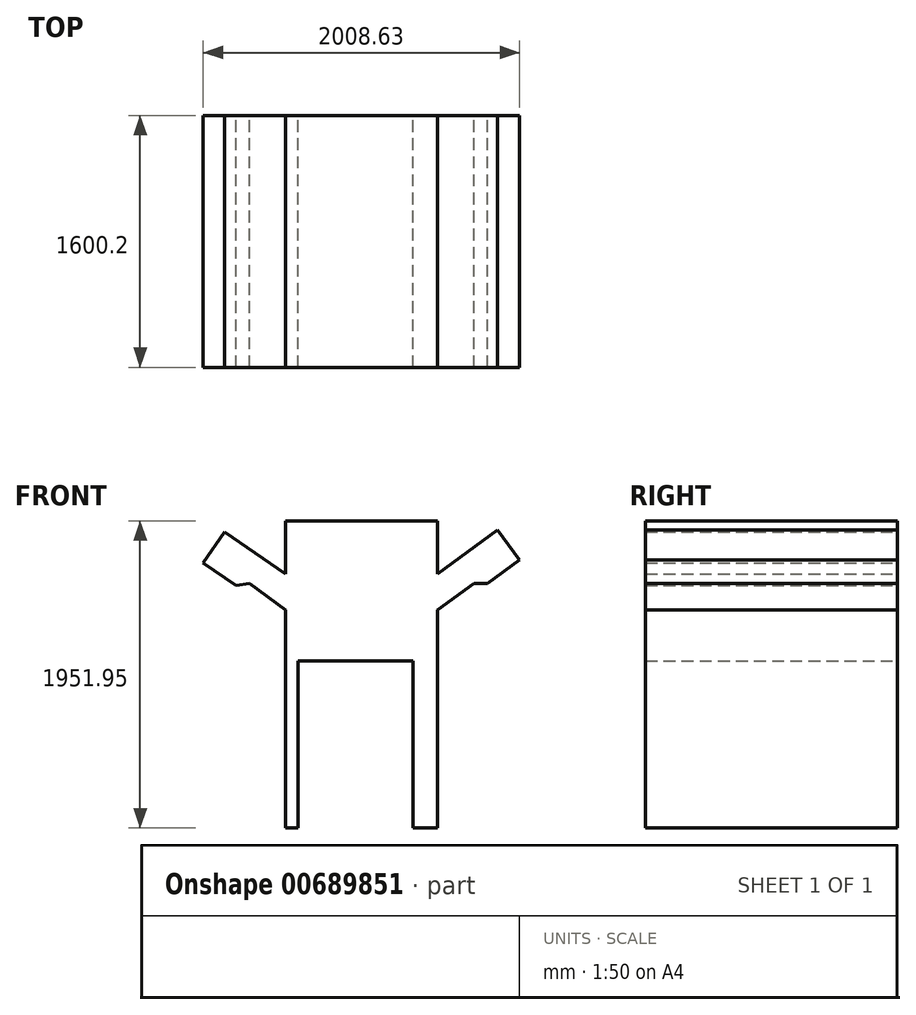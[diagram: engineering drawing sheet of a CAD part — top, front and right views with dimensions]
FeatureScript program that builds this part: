
annotation { "Feature Type Name" : "Feature", "Feature Type Description" : "" }
export const myFeature = defineFeature(function(context is Context, id is Id, definition is map)
    precondition{}
    {
        {
            var Q0;
            Q0=qCreatedBy(makeId("Front.planeOp"),FACE);
            var sketch = newSketch(context, id + "F0", { "sketchPlane" : qUnion([Q0])});
            skLineSegment(sketch, "E0", {"start": v(0, 0) * mm, "end": v(0, 1500) * mm, "construction": true});
            skLineSegment(sketch, "E1.bottom", {"start": v(-1147.27, 0) * mm, "end": v(-1302.33, 0) * mm});
            skLineSegment(sketch, "E1.top", {"start": v(-1147.27, 1951.95) * mm, "end": v(-2112.47, 1951.95) * mm});
            skLineSegment(sketch, "E1.left", {"start": v(-1147.27, 0) * mm, "end": v(-1147.27, 1384.3) * mm});
            skLineSegment(sketch, "E1.right", {"start": v(-2112.47, 0) * mm, "end": v(-2112.47, 1384.3) * mm});
            skLineSegment(sketch, "E2", {"start": v(-1147.27, 1384.3) * mm, "end": v(-917.57, 1554.27) * mm});
            skLineSegment(sketch, "E3", {"start": v(-917.57, 1554.27) * mm, "end": v(-831.16, 1552.95) * mm});
            skLineSegment(sketch, "E4", {"start": v(-831.16, 1552.95) * mm, "end": v(-626.98, 1704.03) * mm});
            skLineSegment(sketch, "E5", {"start": v(-626.98, 1704.03) * mm, "end": v(-767.5, 1893.92) * mm});
            skLineSegment(sketch, "E6", {"start": v(-767.5, 1893.92) * mm, "end": v(-1147.27, 1612.9) * mm});
            skLineSegment(sketch, "E7", {"start": v(-2112.47, 1612.9) * mm, "end": v(-2501.82, 1880.5) * mm});
            skLineSegment(sketch, "E8", {"start": v(-2501.82, 1880.5) * mm, "end": v(-2635.61, 1685.82) * mm});
            skLineSegment(sketch, "E9", {"start": v(-2635.61, 1685.82) * mm, "end": v(-2426.34, 1541.87) * mm});
            skLineSegment(sketch, "E10", {"start": v(-2426.34, 1541.87) * mm, "end": v(-2342.17, 1554.27) * mm});
            skLineSegment(sketch, "E11", {"start": v(-2342.17, 1554.27) * mm, "end": v(-2112.47, 1384.3) * mm});
            skLineSegment(sketch, "E12.top", {"start": v(-2033.73, 1062.7) * mm, "end": v(-1302.33, 1062.7) * mm});
            skLineSegment(sketch, "E12.left", {"start": v(-2033.73, 0) * mm, "end": v(-2033.73, 1062.7) * mm});
            skLineSegment(sketch, "E12.right", {"start": v(-1302.33, 0) * mm, "end": v(-1302.33, 1062.7) * mm});
            skLineSegment(sketch, "E13.trimOffspring", {"start": v(-2112.47, 1612.9) * mm, "end": v(-2112.47, 1951.95) * mm});
            skLineSegment(sketch, "E14.trimOffspring", {"start": v(-1147.27, 1612.9) * mm, "end": v(-1147.27, 1951.95) * mm});
            skLineSegment(sketch, "E15.trimOffspring", {"start": v(-2033.73, 0) * mm, "end": v(-2112.47, 0) * mm});
            skSolve(sketch);
        }
        {
            var Q0;
            Q0 = qSketchRegion(id + "F0", true);
            extrude(context, id + "F1", {"entities" : qUnion([Q0]), "endBound" : BoundingType.SYMMETRIC, "depth" : 1600.2 * mm, "offsetDistance" : 25.4 * mm});
        }
    });
